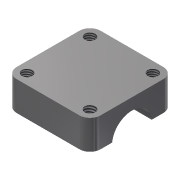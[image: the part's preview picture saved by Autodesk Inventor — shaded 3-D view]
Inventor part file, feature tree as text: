
AUTODESK INVENTOR PART (.ipt)
format: ipt  version: 2015 (Build 190159000, 159)  size: 136,704 bytes
history: native  units: mm
features: hole x5, extrude x1, fillet x1, sketch x1
ambient origin geometry x8: Origin, YZ Plane, XZ Plane, XY Plane, X Axis, Y Axis, Z Axis, Center Point
bodies: Body1 (feature_tree)
feature tree (8):
  extrude  "Extrusion2"  Depth=40.0mm
  hole  "Hole3"  [1 undecoded]
  hole  "Hole4"  [1 undecoded]
  hole  "Hole5"  [1 undecoded]
  hole  "Hole6"  [1 undecoded]
  hole  "Hole7"  [1 undecoded]
  fillet  "Fillet1"  [1 undecoded]
  sketch  "Sketch4"  dims[d37=40.0mm d38=40.0mm d39=14.0mm d40=0.0mm d50=5.0mm d51=5.0mm d52=4.917mm d53=12.0mm d54=9.0mm d55=8.0mm d56=90.0deg d57=17.1mm d58=20.594885mm d59=5.0mm d60=5.0mm d61=4.917mm d62=12.0mm d63=9.0mm d64=8.0mm d65=90.0deg d66=17.1mm d67=20.594885mm d68=5.0mm d69=5.0mm d70=4.978mm d71=12.7mm d72=9.0mm d73=8.0mm d74=90.0deg d75=19.05mm d76=20.594885mm d77=5.0mm d78=5.0mm d79=4.917mm d80=12.0mm d81=9.0mm d82=8.0mm d83=90.0deg d84=17.1mm d85=20.594885mm d86=15.0mm d87=20.0mm d88=19.0mm d89=6.0mm d90=4.0mm d91=2.0mm d92=90.0deg d93=8.0mm d94=20.594885mm d95=5.0mm]
note: 6 required parameter values undecoded (feature->parameter linkage not recoverable at this tier; creation-order binding heuristic only, values carry confidence <= 0.55)
